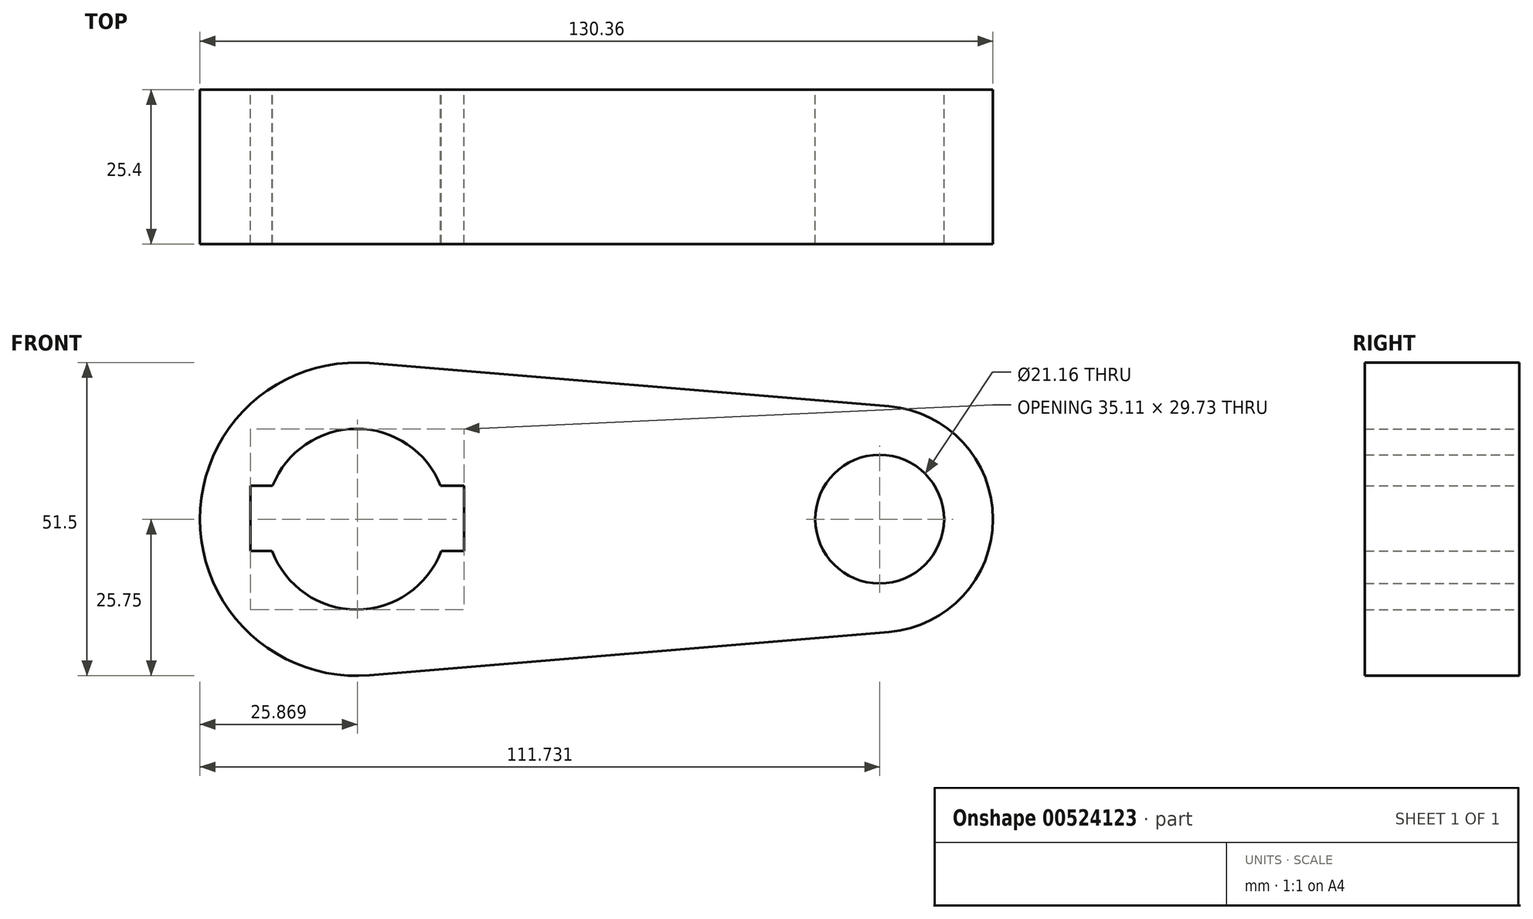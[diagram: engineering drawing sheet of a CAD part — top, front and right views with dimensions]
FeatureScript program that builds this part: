
annotation { "Feature Type Name" : "Feature", "Feature Type Description" : "" }
export const myFeature = defineFeature(function(context is Context, id is Id, definition is map)
    precondition{}
    {
        {
            var Q0;
            Q0=qCreatedBy(makeId("Front.planeOp"),FACE);
            var sketch = newSketch(context, id + "F0", { "sketchPlane" : qUnion([Q0])});
            skCircle(sketch, "E0", {"center": v(0, 0) * mm, "radius": 25.75 * mm});
            skCircle(sketch, "E1", {"center": v(0, 0) * mm, "radius": 14.87 * mm});
            skLineSegment(sketch, "E2.bottom", {"start": v(-17.44, 5.5) * mm, "end": v(17.67, 5.5) * mm});
            skLineSegment(sketch, "E2.top", {"start": v(-17.44, -5.25) * mm, "end": v(17.67, -5.25) * mm});
            skLineSegment(sketch, "E2.left", {"start": v(-17.44, 5.5) * mm, "end": v(-17.44, -5.25) * mm});
            skLineSegment(sketch, "E2.right", {"start": v(17.67, 5.5) * mm, "end": v(17.67, -5.25) * mm});
            skCircle(sketch, "E3", {"center": v(85.98, 0) * mm, "radius": 18.63 * mm});
            skCircle(sketch, "E4", {"center": v(85.98, 0) * mm, "radius": 10.58 * mm});
            skLineSegment(sketch, "E5", {"start": v(2.13, 25.67) * mm, "end": v(87.52, 18.57) * mm});
            skLineSegment(sketch, "E6", {"start": v(2.13, -25.67) * mm, "end": v(87.52, -18.57) * mm});
            skSolve(sketch);
        }
        {
            var Q0;
            {var subQ11=sQuery(id+"F0.wireOp",EDGE,"E2.left");Q0=makeQuery(id+"F0.imprint","IMPRINT",FACE,{"disambiguationData":[TD([[makeQuery(id+"F0.imprint","IMPRINT",EDGE,{"derivedFrom":subQ11}),-1.0]])]});}
            var Q1;
            {var subQ0=sQuery(id+"F0.wireOp",EDGE,"E5");Q1=makeQuery(id+"F0.imprint","IMPRINT",FACE,{"disambiguationData":[TD([[makeQuery(id+"F0.imprint","IMPRINT",EDGE,{"derivedFrom":subQ0}),-1.0]])]});}
            var Q2;
            Q2=makeQuery(id+"F0.imprint","IMPRINT",FACE,{"disambiguationData":[TD([[makeQuery(id+"F0.imprint","IMPRINT",EDGE,{"derivedFrom":sQuery(id+"F0.wireOp",EDGE,"E4")}),-1.0]])]});
            extrude(context, id + "F1", {"entities" : qUnion([Q0, Q1, Q2]), "depth" : 25.4 * mm, "offsetDistance" : 25.4 * mm});
        }
    });
